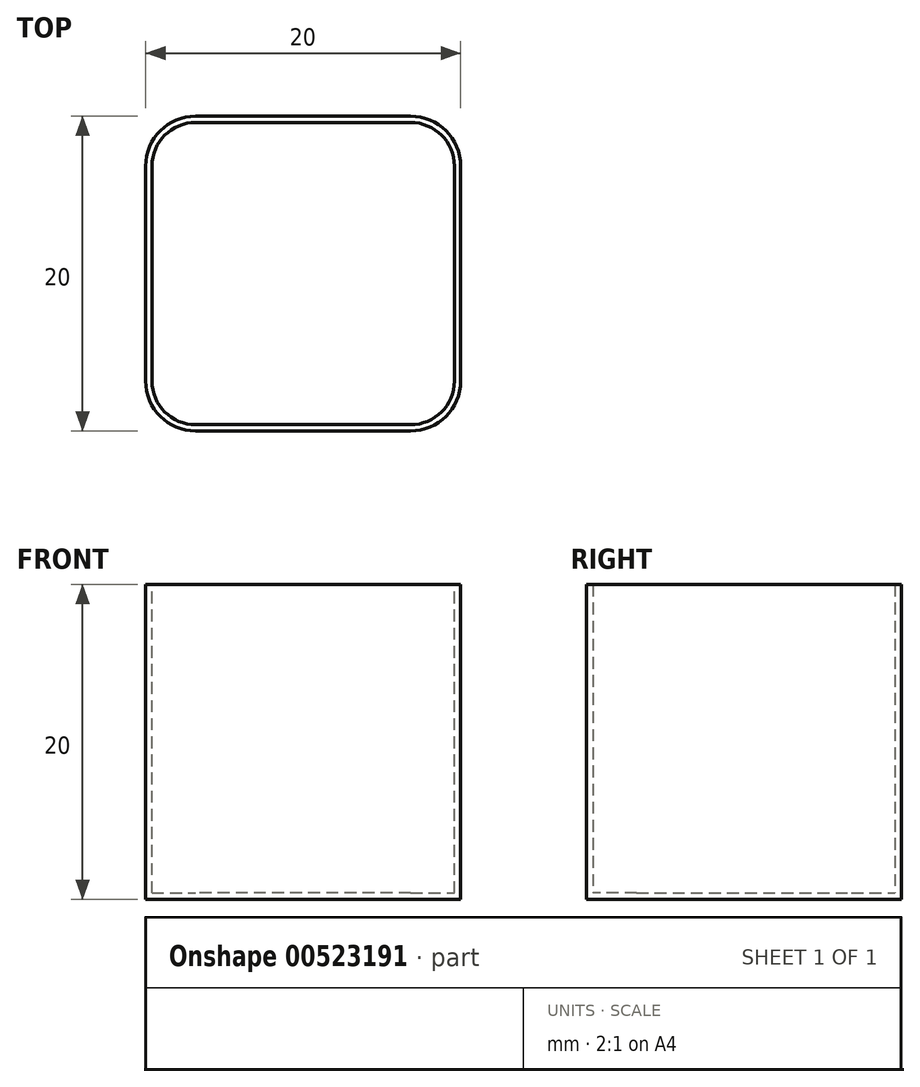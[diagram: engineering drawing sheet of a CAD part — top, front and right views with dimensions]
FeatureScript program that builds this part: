
annotation { "Feature Type Name" : "Feature", "Feature Type Description" : "" }
export const myFeature = defineFeature(function(context is Context, id is Id, definition is map)
    precondition{}
    {
        {
            var Q0;
            Q0=qCreatedBy(makeId("Top.planeOp"),FACE);
            var sketch = newSketch(context, id + "F0", { "sketchPlane" : qUnion([Q0])});
            skLineSegment(sketch, "E0.bottom", {"start": v(10, -10) * mm, "end": v(-10, -10) * mm});
            skLineSegment(sketch, "E0.top", {"start": v(10, 10) * mm, "end": v(-10, 10) * mm});
            skLineSegment(sketch, "E0.left", {"start": v(10, -10) * mm, "end": v(10, 10) * mm});
            skLineSegment(sketch, "E0.right", {"start": v(-10, -10) * mm, "end": v(-10, 10) * mm});
            skPoint(sketch, "E0.middle", {"position": v(0, 0) * mm});
            skSolve(sketch);
        }
        {
            var Q0;
            Q0=makeQuery(id+"F0.imprint","IMPRINT",FACE,{"disambiguationData":[TD([[makeQuery(id+"F0.imprint","IMPRINT",EDGE,{"derivedFrom":sQuery(id+"F0.wireOp",EDGE,"E0.bottom")}),-1.0]])]});
            extrude(context, id + "F1", {"entities" : qUnion([Q0]), "depth" : 20 * mm, "offsetDistance" : 25.4 * mm});
        }
        {
            var Q0;
            Q0=makeQuery(id+"F1.opExtrude","SWEPT_EDGE",EDGE,{"disambiguationData":[OSD([sQuery(id+"F0.wireOp",EDGE,"E0.bottom"),sQuery(id+"F0.wireOp",EDGE,"E0.right")])]});
            var Q1;
            Q1=makeQuery(id+"F1.opExtrude","SWEPT_EDGE",EDGE,{"disambiguationData":[OSD([sQuery(id+"F0.wireOp",EDGE,"E0.bottom"),sQuery(id+"F0.wireOp",EDGE,"E0.left")])]});
            var Q2;
            Q2=makeQuery(id+"F1.opExtrude","SWEPT_EDGE",EDGE,{"disambiguationData":[OSD([sQuery(id+"F0.wireOp",EDGE,"E0.top"),sQuery(id+"F0.wireOp",EDGE,"E0.left")])]});
            var Q3;
            Q3=makeQuery(id+"F1.opExtrude","SWEPT_EDGE",EDGE,{"disambiguationData":[OSD([sQuery(id+"F0.wireOp",EDGE,"E0.top"),sQuery(id+"F0.wireOp",EDGE,"E0.right")])]});
            fillet(context, id + "F2", {"entities" : qUnion([Q0, Q1, Q2, Q3]), "radius" : 3.17 * mm, "tangentPropagation" : true, "allowEdgeOverflow" : false});
        }
        {
            var Q0;
            Q0=makeQuery(id+"F1.opExtrude","CAP_FACE",FACE,{"disambiguationData":[OSD([sQuery(id+"F0.wireOp",EDGE,"E0.bottom"),sQuery(id+"F0.wireOp",EDGE,"E0.top"),sQuery(id+"F0.wireOp",EDGE,"E0.left"),sQuery(id+"F0.wireOp",EDGE,"E0.right")])],"isStart":false});
            shell(context, id + "F3", {"entities" : qUnion([Q0]), "thickness" : .4 * mm});
        }
    });
